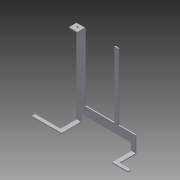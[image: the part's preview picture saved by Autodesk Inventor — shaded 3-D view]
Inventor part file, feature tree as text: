
AUTODESK INVENTOR PART (.ipt)
format: ipt  version: 2013 (Build 170138000, 138)  size: 266,752 bytes
history: native  units: in
note: dims shown in document units (in); Inventor stores cm internally (conversion verified against a paired STEP export)
features: sheet_metal_op x11, other x7, sketch x6, projected_geometry x1
ambient origin geometry x8: Origin, YZ Plane, XZ Plane, XY Plane, X Axis, Y Axis, Z Axis, Center Point
bodies: Solid1 (feature_tree)
feature tree (25):
  sheet_metal_op  "Face1"
  sheet_metal_op  "Flange1"
  sheet_metal_op  "Flange2"
  sheet_metal_op  "Face2"
  sheet_metal_op  "Face4"
  sketch  "Sketch1"  dims[d0=8.0in]
  other  "Plate1"
  sketch  "Sketch2"  dims[d1=1.0in]
  other  "Plate2"
  sheet_metal_op  "Bend1"
  sheet_metal_op  "Corner1"
  sketch  "Sketch3"  dims[d2=5.95in]
  other  "Plate3"
  sheet_metal_op  "Bend2"
  sheet_metal_op  "Corner2"
  sketch  "Sketch4"  dims[d3=1.0in]
  sketch  "Sketch5"  dims[d4=1.0in]
  projected_geometry  "Projected Loop1"
  other  "Plate4"
  sheet_metal_op  "Bend3"
  sketch  "Sketch7"  dims[d5=0.5in d6=1.0in d7=0.5in d8=0.0in d9=1.0in d10=1.0in d11=0.125in d12=0.125in d13=0.0625in d14=0.25in d15=0.125in d16=2.375in d17=90.0deg d18=0.05in d19=0.5in d20=0.125in d21=0.125in d22=0.125in d23=0.0625in d24=0.25in d25=0.125in d26=1.0in d27=90.0deg d28=0.05in d29=0.5in d30=0.125in d31=0.125in d32=0.19in d33=0.5in d34=0.5in d35=0.125in d36=0.0in d37=3.0in d38=0.375in d39=1.375in d40=0.375in d41=0.125in d42=0.125in d43=0.0625in d44=0.25in d45=0.125in d55=0.125in d56=0.125in d57=0.0625in d58=0.25in d59=0.125in d60=0.5in d61=2.0in d62=7.825in]
  other  "Plate6"
  sheet_metal_op  "Bend5"
  other  "Cut1"
  other  "Definition1"
